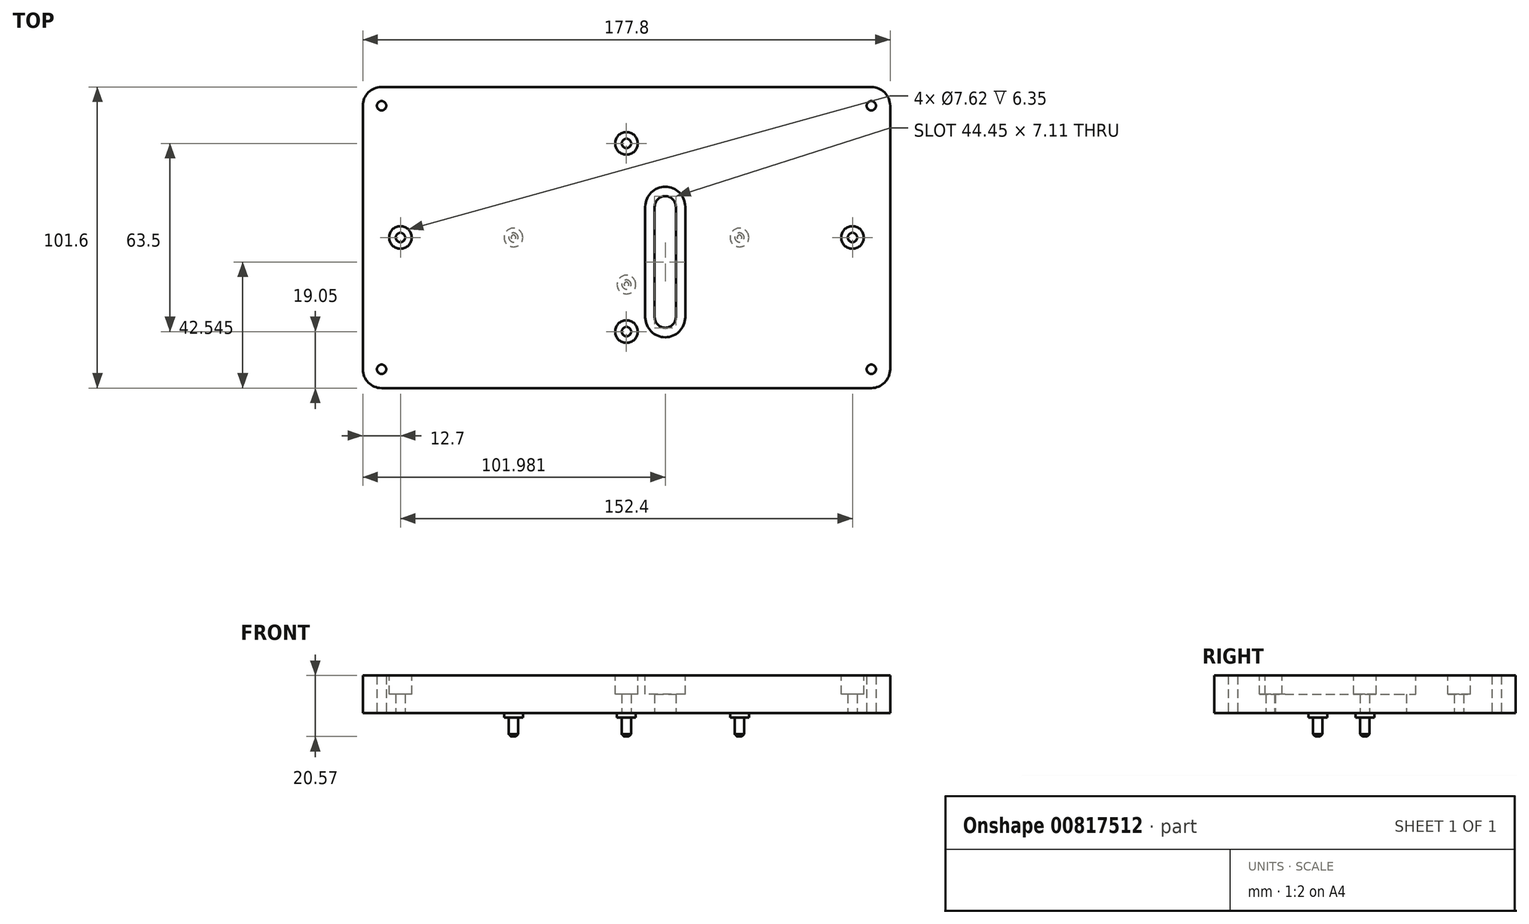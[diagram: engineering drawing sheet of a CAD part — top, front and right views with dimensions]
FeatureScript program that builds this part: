
annotation { "Feature Type Name" : "Feature", "Feature Type Description" : "" }
export const myFeature = defineFeature(function(context is Context, id is Id, definition is map)
    precondition{}
    {
        {
            var Q0;
            Q0=qCreatedBy(makeId("Top.planeOp"),FACE);
            var sketch = newSketch(context, id + "F0", { "sketchPlane" : qUnion([Q0])});
            skLineSegment(sketch, "E0.bottom", {"start": v(-88.9, 50.8) * mm, "end": v(88.9, 50.8) * mm});
            skLineSegment(sketch, "E0.top", {"start": v(-88.9, -50.8) * mm, "end": v(88.9, -50.8) * mm});
            skLineSegment(sketch, "E0.left", {"start": v(-88.9, 50.8) * mm, "end": v(-88.9, -50.8) * mm});
            skLineSegment(sketch, "E0.right", {"start": v(88.9, 50.8) * mm, "end": v(88.9, -50.8) * mm});
            skLineSegment(sketch, "E1", {"start": v(-62.24, 0) * mm, "end": v(80.27, 0) * mm, "construction": true});
            skSolve(sketch);
        }
        {
            var Q0;
            Q0 = qSketchRegion(id + "F0", true);
            extrude(context, id + "F1", {"entities" : qUnion([Q0]), "depth" : 12.7 * mm, "offsetDistance" : 25.4 * mm});
        }
        {
            var Q0;
            Q0=qCreatedBy(makeId("Top.planeOp"),FACE);
            var sketch = newSketch(context, id + "F2", { "sketchPlane" : qUnion([Q0])});
            skCircle(sketch, "E2", {"center": v(-38.1, 0) * mm, "radius": 3.18 * mm});
            skCircle(sketch, "E3", {"center": v(38.1, 0) * mm, "radius": 3.18 * mm});
            skCircle(sketch, "E4", {"center": v(0, -15.88) * mm, "radius": 3.18 * mm});
            skSolve(sketch);
        }
        {
            var Q0;
            Q0 = qSketchRegion(id + "F2", true);
            extrude(context, id + "F3", {"entities" : qUnion([Q0]), "operationType" : NewBodyOperationType.ADD, "oppositeDirection" : true, "depth" : 1.52 * mm, "offsetDistance" : 25.4 * mm});
        }
        {
            var Q0;
            Q0=makeQuery(id+"F3.opExtrude","CAP_FACE",FACE,{"disambiguationData":[OSD([sQuery(id+"F2.wireOp",EDGE,"E2")])],"isStart":false});
            var sketch = newSketch(context, id + "F4", { "sketchPlane" : qUnion([Q0])});
            skCircle(sketch, "E5", {"center": v(-38.1, 0) * mm, "radius": 1.56 * mm});
            skCircle(sketch, "E6", {"center": v(38.1, 0) * mm, "radius": 1.56 * mm});
            skCircle(sketch, "E7", {"center": v(0, 15.88) * mm, "radius": 1.56 * mm});
            skSolve(sketch);
        }
        {
            var Q0;
            Q0 = qSketchRegion(id + "F4", true);
            extrude(context, id + "F5", {"entities" : qUnion([Q0]), "operationType" : NewBodyOperationType.ADD, "depth" : 6.35 * mm, "offsetDistance" : 25.4 * mm});
        }
        {
            var Q0;
            Q0=makeQuery(id+"F5.opExtrude","CAP_EDGE",EDGE,{"disambiguationData":[OSD([sQuery(id+"F4.wireOp",EDGE,"E5")])],"isStart":false});
            var Q1;
            Q1=makeQuery(id+"F5.opExtrude","CAP_EDGE",EDGE,{"disambiguationData":[OSD([sQuery(id+"F4.wireOp",EDGE,"E7")])],"isStart":false});
            var Q2;
            Q2=makeQuery(id+"F5.opExtrude","CAP_EDGE",EDGE,{"disambiguationData":[OSD([sQuery(id+"F4.wireOp",EDGE,"E6")])],"isStart":false});
            chamfer(context, id + "F6", {"entities" : qUnion([Q0, Q1, Q2]), "width" : 0.76 * mm, "tangentPropagation" : true});
        }
        {
            var Q0;
            Q0=makeQuery(id+"F1.opExtrude","SWEPT_EDGE",EDGE,{"disambiguationData":[OSD([sQuery(id+"F0.wireOp",EDGE,"E0.top"),sQuery(id+"F0.wireOp",EDGE,"E0.left")])]});
            var Q1;
            Q1=makeQuery(id+"F1.opExtrude","SWEPT_EDGE",EDGE,{"disambiguationData":[OSD([sQuery(id+"F0.wireOp",EDGE,"E0.top"),sQuery(id+"F0.wireOp",EDGE,"E0.right")])]});
            var Q2;
            Q2=makeQuery(id+"F1.opExtrude","SWEPT_EDGE",EDGE,{"disambiguationData":[OSD([sQuery(id+"F0.wireOp",EDGE,"E0.bottom"),sQuery(id+"F0.wireOp",EDGE,"E0.right")])]});
            var Q3;
            Q3=makeQuery(id+"F1.opExtrude","SWEPT_EDGE",EDGE,{"disambiguationData":[OSD([sQuery(id+"F0.wireOp",EDGE,"E0.bottom"),sQuery(id+"F0.wireOp",EDGE,"E0.left")])]});
            fillet(context, id + "F7", {"entities" : qUnion([Q0, Q1, Q2, Q3]), "radius" : 6.35 * mm, "tangentPropagation" : true, "allowEdgeOverflow" : false});
        }
        {
            var Q0;
            Q0=makeQuery(id+"F1.opExtrude","CAP_FACE",FACE,{"disambiguationData":[OSD([sQuery(id+"F0.wireOp",EDGE,"E0.bottom"),sQuery(id+"F0.wireOp",EDGE,"E0.top"),sQuery(id+"F0.wireOp",EDGE,"E0.left"),sQuery(id+"F0.wireOp",EDGE,"E0.right")])],"isStart":true});
            var sketch = newSketch(context, id + "F8", { "sketchPlane" : qUnion([Q0])});
            skCircle(sketch, "E8", {"center": v(82.55, 44.45) * mm, "radius": 1.59 * mm});
            skCircle(sketch, "E9", {"center": v(82.55, -44.45) * mm, "radius": 1.59 * mm});
            skCircle(sketch, "E10", {"center": v(-82.55, -44.45) * mm, "radius": 1.59 * mm});
            skCircle(sketch, "E11", {"center": v(-82.55, 44.45) * mm, "radius": 1.59 * mm});
            skSolve(sketch);
        }
        {
            var Q0;
            Q0 = qSketchRegion(id + "F8", true);
            extrude(context, id + "F9", {"entities" : qUnion([Q0]), "operationType" : NewBodyOperationType.REMOVE, "endBound" : BoundingType.THROUGH_ALL, "oppositeDirection" : true, "depth" : 25.4 * mm, "offsetDistance" : 25.4 * mm});
        }
        {
            var Q0;
            Q0=makeQuery(id+"F1.opExtrude","CAP_FACE",FACE,{"disambiguationData":[OSD([sQuery(id+"F0.wireOp",EDGE,"E0.bottom"),sQuery(id+"F0.wireOp",EDGE,"E0.top"),sQuery(id+"F0.wireOp",EDGE,"E0.left"),sQuery(id+"F0.wireOp",EDGE,"E0.right")])],"isStart":true});
            var sketch = newSketch(context, id + "F10", { "sketchPlane" : qUnion([Q0])});
            skCircle(sketch, "E12", {"center": v(0, 31.75) * mm, "radius": 1.59 * mm});
            skCircle(sketch, "E13", {"center": v(0, -31.75) * mm, "radius": 1.59 * mm});
            skSolve(sketch);
        }
        {
            var Q0;
            Q0 = qSketchRegion(id + "F10", true);
            extrude(context, id + "F11", {"entities" : qUnion([Q0]), "operationType" : NewBodyOperationType.REMOVE, "endBound" : BoundingType.THROUGH_ALL, "oppositeDirection" : true, "depth" : 25.4 * mm, "offsetDistance" : 25.4 * mm});
        }
        {
            var Q0;
            Q0=makeQuery(id+"F1.opExtrude","CAP_FACE",FACE,{"disambiguationData":[OSD([sQuery(id+"F0.wireOp",EDGE,"E0.bottom"),sQuery(id+"F0.wireOp",EDGE,"E0.top"),sQuery(id+"F0.wireOp",EDGE,"E0.left"),sQuery(id+"F0.wireOp",EDGE,"E0.right")])],"isStart":false});
            var sketch = newSketch(context, id + "F12", { "sketchPlane" : qUnion([Q0])});
            skCircle(sketch, "E14", {"center": v(0, 31.75) * mm, "radius": 3.81 * mm});
            skCircle(sketch, "E15", {"center": v(0, -31.75) * mm, "radius": 3.81 * mm});
            skSolve(sketch);
        }
        {
            var Q0;
            Q0 = qSketchRegion(id + "F12", true);
            extrude(context, id + "F13", {"entities" : qUnion([Q0]), "operationType" : NewBodyOperationType.REMOVE, "oppositeDirection" : true, "depth" : 6.35 * mm, "offsetDistance" : 25.4 * mm});
        }
        {
            var Q0;
            Q0=makeQuery(id+"F1.opExtrude","CAP_FACE",FACE,{"disambiguationData":[OSD([sQuery(id+"F0.wireOp",EDGE,"E0.bottom"),sQuery(id+"F0.wireOp",EDGE,"E0.top"),sQuery(id+"F0.wireOp",EDGE,"E0.left"),sQuery(id+"F0.wireOp",EDGE,"E0.right")])],"isStart":true});
            var sketch = newSketch(context, id + "F14", { "sketchPlane" : qUnion([Q0])});
            skLineSegment(sketch, "E16.left", {"start": v(9.52, 26.92) * mm, "end": v(9.52, -10.41) * mm});
            skLineSegment(sketch, "E16.right", {"start": v(16.64, 26.92) * mm, "end": v(16.64, -10.41) * mm});
            skArc(sketch, "E17", {"start": v(16.64, 26.92) * mm, "mid": v(13.08, 30.48) * mm, "end": v(9.52, 26.92) * mm});
            skPoint(sketch, "E17.first.point", {"position": v(9.52, 26.92) * mm});
            skPoint(sketch, "E17.second.point", {"position": v(16.64, 26.92) * mm});
            skPoint(sketch, "E17.third.point", {"position": v(13.08, 30.48) * mm});
            skArc(sketch, "E18", {"start": v(9.52, -10.41) * mm, "mid": v(13.08, -13.97) * mm, "end": v(16.64, -10.41) * mm});
            skPoint(sketch, "E18.first.point", {"position": v(9.52, -10.41) * mm});
            skPoint(sketch, "E18.second.point", {"position": v(16.64, -10.41) * mm});
            skPoint(sketch, "E18.third.point", {"position": v(13.08, -13.97) * mm});
            skPoint(sketch, "E19.orphan", {"position": v(9.52, 30.48) * mm});
            skPoint(sketch, "E20.orphan", {"position": v(16.64, 30.48) * mm});
            skPoint(sketch, "E21.orphan", {"position": v(9.52, -13.97) * mm});
            skPoint(sketch, "E22.orphan", {"position": v(16.64, -13.97) * mm});
            skSolve(sketch);
        }
        {
            var Q0;
            Q0 = qSketchRegion(id + "F14", true);
            extrude(context, id + "F15", {"entities" : qUnion([Q0]), "operationType" : NewBodyOperationType.REMOVE, "endBound" : BoundingType.THROUGH_ALL, "oppositeDirection" : true, "depth" : 25.4 * mm, "offsetDistance" : 25.4 * mm});
        }
        {
            var Q0;
            Q0=makeQuery(id+"F1.opExtrude","CAP_FACE",FACE,{"disambiguationData":[OSD([sQuery(id+"F0.wireOp",EDGE,"E0.bottom"),sQuery(id+"F0.wireOp",EDGE,"E0.top"),sQuery(id+"F0.wireOp",EDGE,"E0.left"),sQuery(id+"F0.wireOp",EDGE,"E0.right")])],"isStart":false});
            var sketch = newSketch(context, id + "F16", { "sketchPlane" : qUnion([Q0])});
            skLineSegment(sketch, "E23.0", {"start": v(19.81, 10.41) * mm, "end": v(19.81, -26.92) * mm});
            skArc(sketch, "E23.1", {"start": v(19.81, 10.41) * mm, "mid": v(13.08, 17.15) * mm, "end": v(6.35, 10.41) * mm});
            skLineSegment(sketch, "E23.2", {"start": v(6.35, 10.41) * mm, "end": v(6.35, -26.92) * mm});
            skArc(sketch, "E23.3", {"start": v(6.35, -26.92) * mm, "mid": v(13.08, -33.65) * mm, "end": v(19.81, -26.92) * mm});
            skSolve(sketch);
        }
        {
            var Q0;
            Q0 = qSketchRegion(id + "F16", true);
            extrude(context, id + "F17", {"entities" : qUnion([Q0]), "operationType" : NewBodyOperationType.REMOVE, "oppositeDirection" : true, "depth" : 6.35 * mm, "offsetDistance" : 25.4 * mm});
        }
        {
            var Q0;
            Q0=makeQuery(id+"F1.opExtrude","CAP_FACE",FACE,{"disambiguationData":[OSD([sQuery(id+"F0.wireOp",EDGE,"E0.bottom"),sQuery(id+"F0.wireOp",EDGE,"E0.top"),sQuery(id+"F0.wireOp",EDGE,"E0.left"),sQuery(id+"F0.wireOp",EDGE,"E0.right")])],"isStart":true});
            var sketch = newSketch(context, id + "F18", { "sketchPlane" : qUnion([Q0])});
            skCircle(sketch, "E24", {"center": v(76.2, 0) * mm, "radius": 1.59 * mm});
            skCircle(sketch, "E25", {"center": v(-76.2, 0) * mm, "radius": 1.59 * mm});
            skCircle(sketch, "E26", {"center": v(38.1, 0) * mm, "radius": 3.84 * mm, "construction": true});
            skSolve(sketch);
        }
        {
            var Q0;
            Q0 = qSketchRegion(id + "F18", true);
            extrude(context, id + "F19", {"entities" : qUnion([Q0]), "operationType" : NewBodyOperationType.REMOVE, "endBound" : BoundingType.THROUGH_ALL, "oppositeDirection" : true, "depth" : 25.4 * mm, "offsetDistance" : 25.4 * mm});
        }
        {
            var Q0;
            Q0=makeQuery(id+"F1.opExtrude","CAP_FACE",FACE,{"disambiguationData":[OSD([sQuery(id+"F0.wireOp",EDGE,"E0.bottom"),sQuery(id+"F0.wireOp",EDGE,"E0.top"),sQuery(id+"F0.wireOp",EDGE,"E0.left"),sQuery(id+"F0.wireOp",EDGE,"E0.right")])],"isStart":false});
            var sketch = newSketch(context, id + "F20", { "sketchPlane" : qUnion([Q0])});
            skCircle(sketch, "E27", {"center": v(-76.2, 0) * mm, "radius": 3.81 * mm});
            skCircle(sketch, "E28", {"center": v(76.2, 0) * mm, "radius": 3.81 * mm});
            skSolve(sketch);
        }
        {
            var Q0;
            Q0 = qSketchRegion(id + "F20", true);
            extrude(context, id + "F21", {"entities" : qUnion([Q0]), "operationType" : NewBodyOperationType.REMOVE, "oppositeDirection" : true, "depth" : 6.35 * mm, "offsetDistance" : 25.4 * mm});
        }
    });
